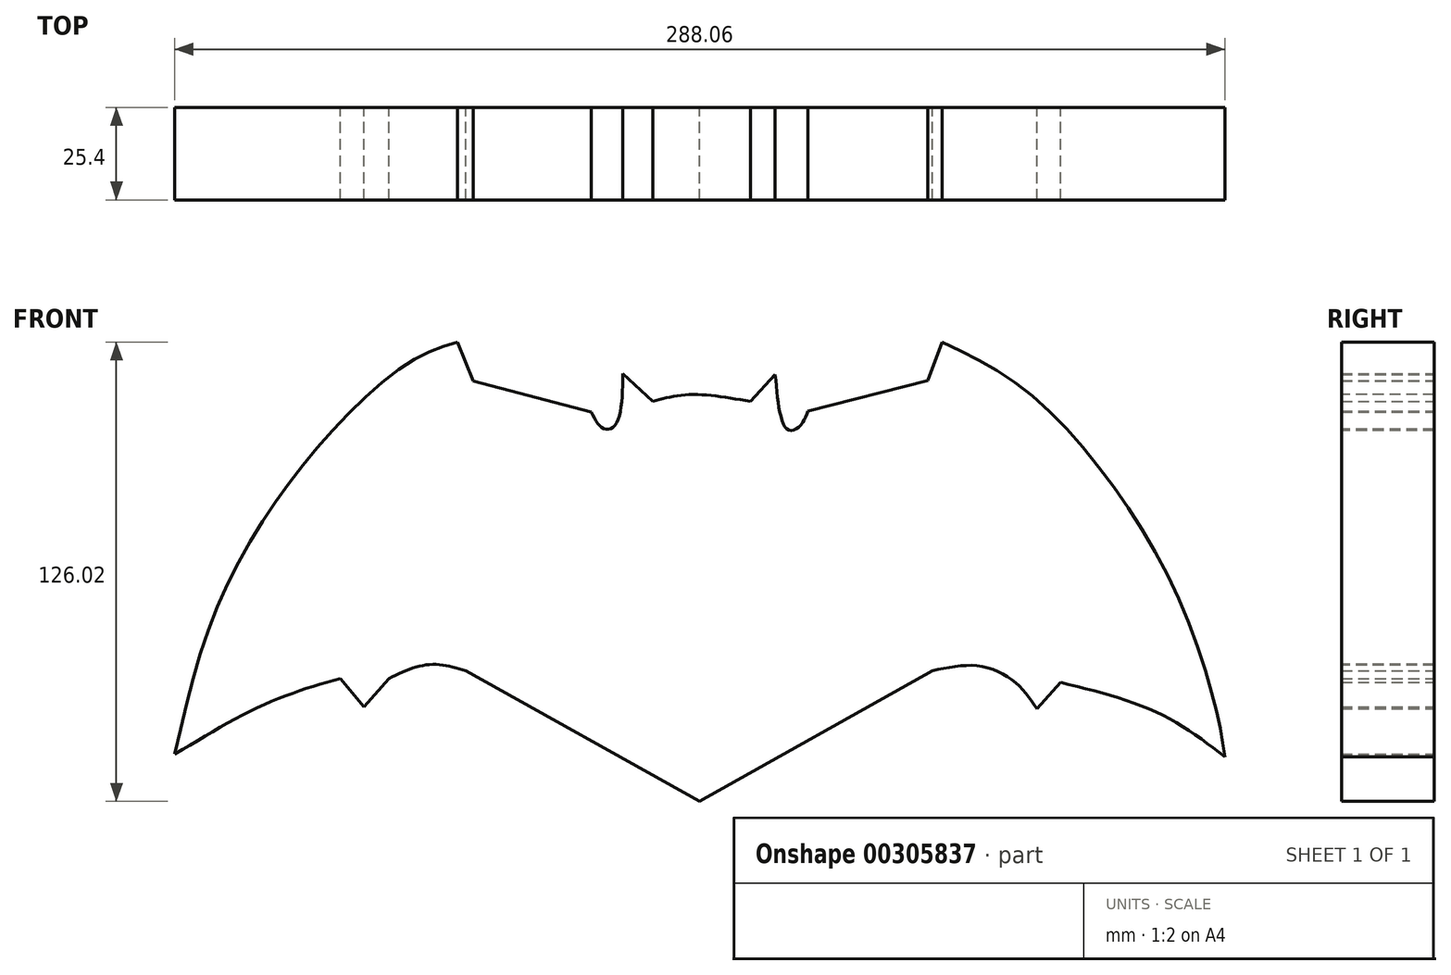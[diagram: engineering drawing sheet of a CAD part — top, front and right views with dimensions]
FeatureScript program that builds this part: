
annotation { "Feature Type Name" : "Feature", "Feature Type Description" : "" }
export const myFeature = defineFeature(function(context is Context, id is Id, definition is map)
    precondition{}
    {
        {
            var Q0;
            Q0=qCreatedBy(makeId("Front.planeOp"),FACE);
            var sketch = newSketch(context, id + "F0", { "sketchPlane" : qUnion([Q0])});
            skLineSegment(sketch, "E0", {"start": v(-53.18, 57.87) * mm, "end": v(-20.82, 49.36) * mm});
            skFitSpline(sketch, "E1", {"points": [v(-20.82, 49.36) * mm, v(-17.4, 44.8) * mm, v(-14.17, 45.75) * mm, v(-12.08, 59.8) * mm], "startDerivative": vector(10.22, -19.72) * mm, "endDerivative": vector(0.87, 37.28) * mm});
            skFitSpline(sketch, "E2", {"points": [v(-12.08, 59.8) * mm, v(-3.9, 52.2) * mm], "startDerivative": vector(8.17, -7.6) * mm, "endDerivative": vector(8.17, -7.6) * mm});
            skFitSpline(sketch, "E3", {"points": [v(-3.9, 52.2) * mm, v(6.16, 54.1) * mm, v(22.88, 52.2) * mm], "startDerivative": vector(21.48, 6.03) * mm, "endDerivative": vector(31.67, -5.55) * mm});
            skLineSegment(sketch, "E4", {"start": v(22.88, 52.2) * mm, "end": v(29.72, 59.62) * mm});
            skFitSpline(sketch, "E5", {"points": [v(29.72, 59.62) * mm, v(31.43, 47.46) * mm, v(33.71, 44.23) * mm, v(36.75, 45.75) * mm, v(38.65, 49.55) * mm], "startDerivative": vector(3.1, -36.51) * mm, "endDerivative": vector(6.49, 18.6) * mm});
            skFitSpline(sketch, "E6", {"points": [v(38.65, 49.55) * mm, v(71.52, 57.9) * mm], "startDerivative": vector(32.87, 8.36) * mm, "endDerivative": vector(32.87, 8.36) * mm});
            skFitSpline(sketch, "E7", {"points": [v(71.52, 57.9) * mm, v(75.5, 68.5) * mm], "startDerivative": vector(3.99, 10.59) * mm, "endDerivative": vector(3.99, 10.59) * mm});
            skFitSpline(sketch, "E8", {"points": [v(75.5, 68.5) * mm, v(97.17, 56.2) * mm, v(119.96, 32.26) * mm, v(139.53, 0) * mm, v(150.55, -31.76) * mm, v(153.05, -45.25) * mm], "startDerivative": vector(116.07, -55.3) * mm, "endDerivative": vector(12.54, -85.76) * mm});
            skFitSpline(sketch, "E9", {"points": [v(153.05, -45.25) * mm, v(134.4, -33.1) * mm, v(108, -24.92) * mm], "startDerivative": vector(-36.9, 28.12) * mm, "endDerivative": vector(-52.92, 12.81) * mm});
            skFitSpline(sketch, "E10", {"points": [v(108, -24.92) * mm, v(101.54, -32.14) * mm], "startDerivative": vector(-6.46, -7.22) * mm, "endDerivative": vector(-6.46, -7.22) * mm});
            skFitSpline(sketch, "E11", {"points": [v(101.54, -32.14) * mm, v(95.65, -24.92) * mm, v(85.39, -20.37) * mm, v(72.85, -21.7) * mm], "startDerivative": vector(-16.63, 25.02) * mm, "endDerivative": vector(-35.62, -7.75) * mm});
            skLineSegment(sketch, "E12", {"start": v(72.85, -21.7) * mm, "end": v(9.02, -57.53) * mm});
            skLineSegment(sketch, "E13", {"start": v(9.02, -57.53) * mm, "end": v(-55.2, -21.7) * mm});
            skFitSpline(sketch, "E14", {"points": [v(-55.2, -21.7) * mm, v(-65.27, -19.99) * mm, v(-76.3, -23.78) * mm], "startDerivative": vector(-20.7, 6.17) * mm, "endDerivative": vector(-21.47, -10.17) * mm});
            skLineSegment(sketch, "E15", {"start": v(-76.3, -23.78) * mm, "end": v(-83.13, -31.57) * mm});
            skLineSegment(sketch, "E16", {"start": v(-83.13, -31.57) * mm, "end": v(-89.6, -23.78) * mm});
            skFitSpline(sketch, "E17", {"points": [v(-89.6, -23.78) * mm, v(-109.73, -30.62) * mm, v(-135.01, -44.58) * mm], "startDerivative": vector(-42.83, -12.24) * mm, "endDerivative": vector(-47.89, -28.93) * mm});
            skLineSegment(sketch, "E18", {"start": v(-53.18, 57.87) * mm, "end": v(-57.4, 68.5) * mm});
            skFitSpline(sketch, "E19", {"points": [v(-57.4, 68.5) * mm, v(-70.49, 63.1) * mm, v(-91.02, 44.99) * mm, v(-109.54, 21.44) * mm, v(-125.04, -8.35) * mm, v(-135.01, -44.58) * mm], "startDerivative": vector(-88.47, -26.76) * mm, "endDerivative": vector(-36.38, -160.04) * mm});
            skSolve(sketch);
        }
        {
            var Q0;
            Q0 = qSketchRegion(id + "F0", true);
            extrude(context, id + "F1", {"entities" : qUnion([Q0]), "depth" : 25.4 * mm});
        }
    });
